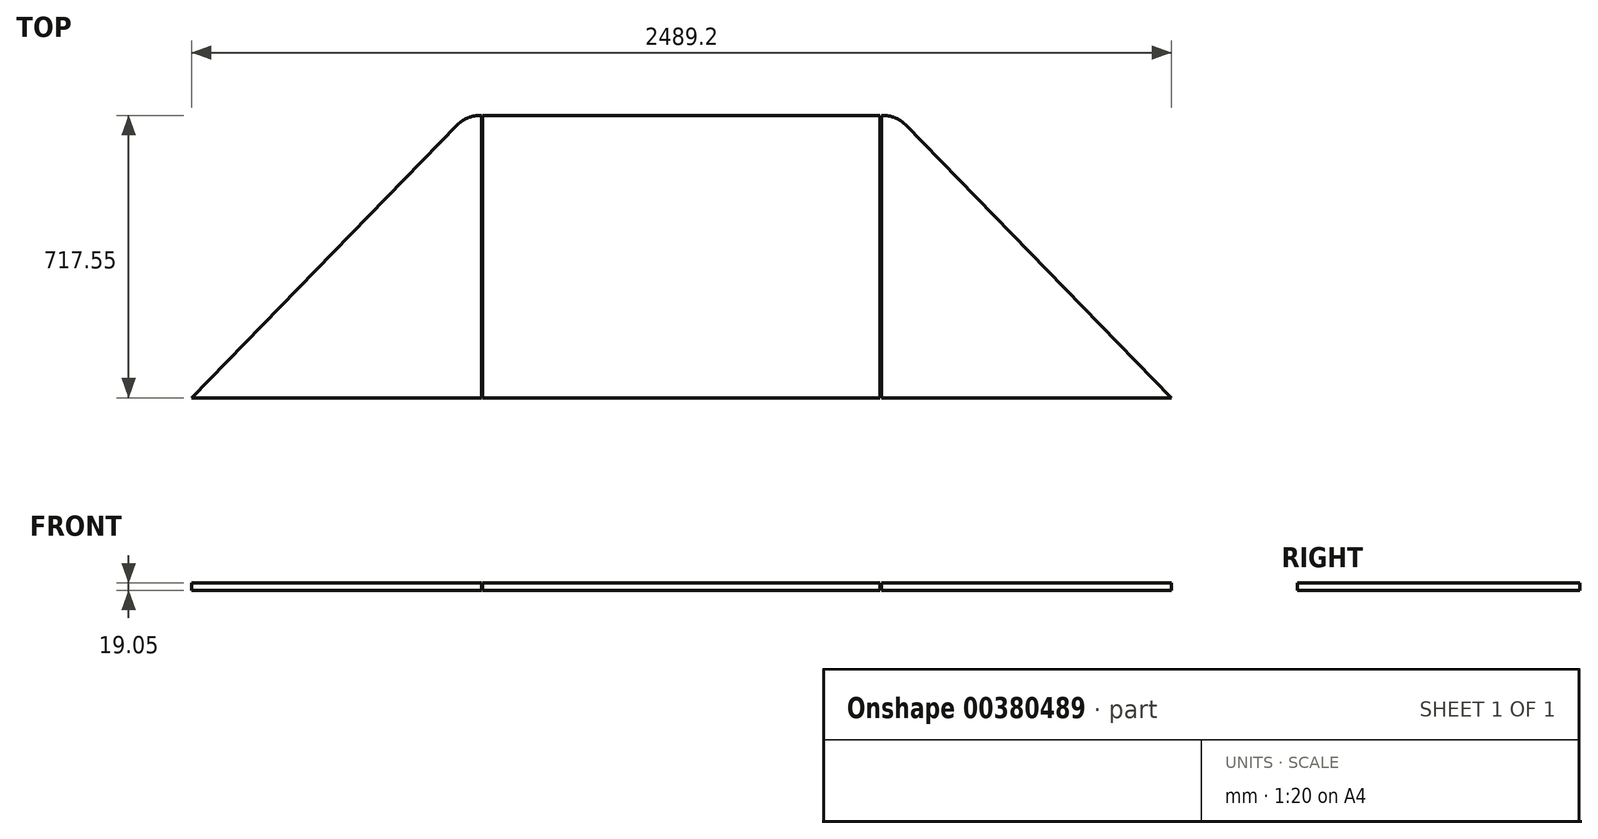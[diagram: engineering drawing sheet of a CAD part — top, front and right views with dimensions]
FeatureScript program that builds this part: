
annotation { "Feature Type Name" : "Feature", "Feature Type Description" : "" }
export const myFeature = defineFeature(function(context is Context, id is Id, definition is map)
    precondition{}
    {
        {
            var Q0;
            Q0=qCreatedBy(makeId("Top.planeOp"),FACE);
            cPlane(context, id + "F0", {"entities" : qUnion([Q0]), "cplaneType" : CPlaneType.OFFSET, "offset" : 425.45 * mm, "oppositeDirection" : true, "width" : 152.4 * mm, "height" : 152.4 * mm});
        }
        {
            var Q0;
            Q0=qCreatedBy(makeId("Top.planeOp"),FACE);
            var sketch = newSketch(context, id + "F1", { "sketchPlane" : qUnion([Q0])});
            skLineSegment(sketch, "E0", {"start": v(-841.8, -705.8) * mm, "end": v(-165.73, -11.3) * mm});
            skLineSegment(sketch, "E1", {"start": v(-111.13, 11.75) * mm, "end": v(-105.2, 11.75) * mm});
            skLineSegment(sketch, "E2", {"start": v(-105.2, 11.75) * mm, "end": v(-105.2, -705.8) * mm});
            skLineSegment(sketch, "E3", {"start": v(-105.2, -705.8) * mm, "end": v(-841.8, -705.8) * mm});
            skLineSegment(sketch, "E4", {"start": v(-102.02, 11.75) * mm, "end": v(-102.02, -705.8) * mm});
            skLineSegment(sketch, "E5", {"start": v(-102.02, -705.8) * mm, "end": v(907.63, -705.8) * mm});
            skLineSegment(sketch, "E6", {"start": v(907.63, -705.8) * mm, "end": v(907.63, 11.75) * mm});
            skLineSegment(sketch, "E7", {"start": v(907.63, 11.75) * mm, "end": v(-102.02, 11.75) * mm});
            skLineSegment(sketch, "E8", {"start": v(910.8, 11.75) * mm, "end": v(910.8, -705.8) * mm});
            skLineSegment(sketch, "E9", {"start": v(910.8, -705.8) * mm, "end": v(1647.4, -705.8) * mm});
            skLineSegment(sketch, "E10", {"start": v(1647.4, -705.8) * mm, "end": v(971.34, -11.3) * mm});
            skLineSegment(sketch, "E11", {"start": v(916.74, 11.75) * mm, "end": v(910.8, 11.75) * mm});
            skPoint(sketch, "E12.visualSharp", {"position": v(-143.3, 11.75) * mm});
            skArc(sketch, "E12.filletArc", {"start": v(-111.13, 11.75) * mm, "mid": v(-140.76, 5.75) * mm, "end": v(-165.73, -11.3) * mm});
            skPoint(sketch, "E13.visualSharp", {"position": v(948.9, 11.75) * mm});
            skArc(sketch, "E13.filletArc", {"start": v(971.34, -11.3) * mm, "mid": v(946.37, 5.75) * mm, "end": v(916.74, 11.75) * mm});
            skSolve(sketch);
        }
        {
            var Q0;
            Q0=makeQuery(id+"F1.imprint","IMPRINT",FACE,{"disambiguationData":[TD([[makeQuery(id+"F1.imprint","IMPRINT",EDGE,{"derivedFrom":sQuery(id+"F1.wireOp",EDGE,"E0")}),-1.0]])]});
            var Q1;
            Q1=makeQuery(id+"F1.imprint","IMPRINT",FACE,{"disambiguationData":[TD([[makeQuery(id+"F1.imprint","IMPRINT",EDGE,{"derivedFrom":sQuery(id+"F1.wireOp",EDGE,"E4")}),1.0]])]});
            var Q2;
            Q2=makeQuery(id+"F1.imprint","IMPRINT",FACE,{"disambiguationData":[TD([[makeQuery(id+"F1.imprint","IMPRINT",EDGE,{"derivedFrom":sQuery(id+"F1.wireOp",EDGE,"E8")}),1.0]])]});
            extrude(context, id + "F2", {"entities" : qUnion([Q0, Q1, Q2]), "depth" : 19.05 * mm});
        }
    });
